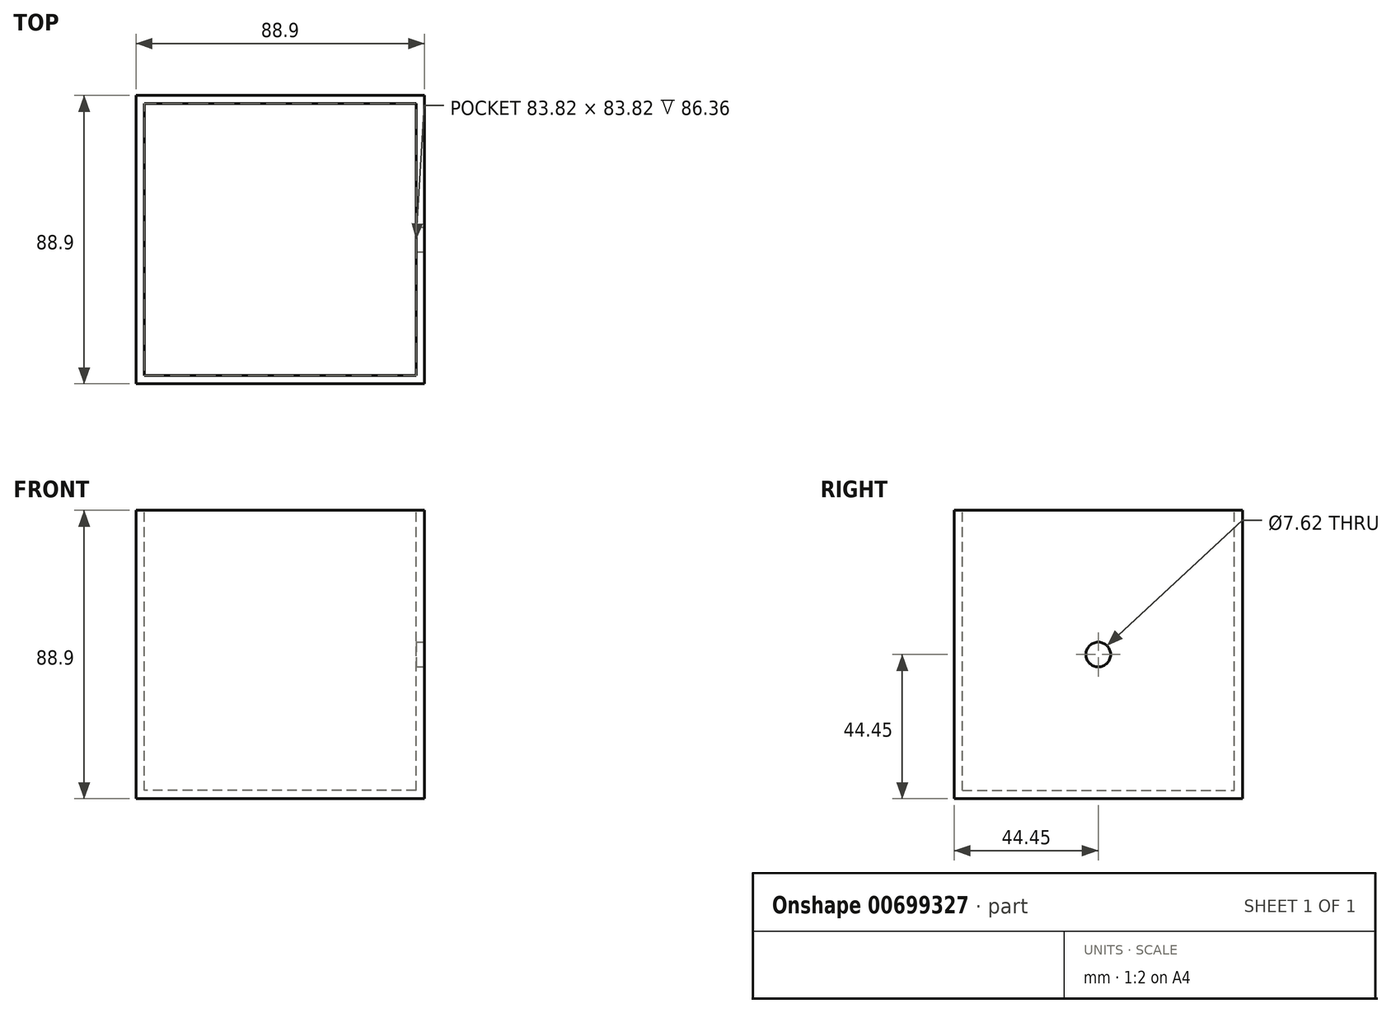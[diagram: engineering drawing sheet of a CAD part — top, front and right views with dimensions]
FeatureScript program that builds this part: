
annotation { "Feature Type Name" : "Feature", "Feature Type Description" : "" }
export const myFeature = defineFeature(function(context is Context, id is Id, definition is map)
    precondition{}
    {
        {
            var Q0;
            Q0=qCreatedBy(makeId("Front.planeOp"),FACE);
            var sketch = newSketch(context, id + "F0", { "sketchPlane" : qUnion([Q0])});
            skLineSegment(sketch, "E0.bottom", {"start": v(44.45, -44.45) * mm, "end": v(-44.45, -44.45) * mm});
            skLineSegment(sketch, "E0.top", {"start": v(44.45, 44.45) * mm, "end": v(-44.45, 44.45) * mm});
            skLineSegment(sketch, "E0.left", {"start": v(44.45, -44.45) * mm, "end": v(44.45, 44.45) * mm});
            skLineSegment(sketch, "E0.right", {"start": v(-44.45, -44.45) * mm, "end": v(-44.45, 44.45) * mm});
            skPoint(sketch, "E0.middle", {"position": v(0, 0) * mm});
            skSolve(sketch);
        }
        {
            var Q0;
            Q0 = qSketchRegion(id + "F0", true);
            extrude(context, id + "F1", {"entities" : qUnion([Q0]), "depth" : 88.9 * mm, "offsetDistance" : 25.4 * mm});
        }
        {
            var Q0;
            Q0=makeQuery(id+"F1.opExtrude","SWEPT_FACE",FACE,{"disambiguationData":[OSD([sQuery(id+"F0.wireOp",EDGE,"E0.top")])]});
            shell(context, id + "F2", {"entities" : qUnion([Q0]), "thickness" : 2.54 * mm});
        }
        {
            var Q0;
            Q0=makeQuery(id+"F1.opExtrude","SWEPT_FACE",FACE,{"disambiguationData":[OSD([sQuery(id+"F0.wireOp",EDGE,"E0.left")])]});
            var sketch = newSketch(context, id + "F3", { "sketchPlane" : qUnion([Q0])});
            skCircle(sketch, "E1", {"center": v(-44.45, 0) * mm, "radius": 3.81 * mm});
            skSolve(sketch);
        }
        {
            var Q0;
            Q0 = qSketchRegion(id + "F3", true);
            extrude(context, id + "F4", {"entities" : qUnion([Q0]), "operationType" : NewBodyOperationType.REMOVE, "oppositeDirection" : true, "depth" : 25.4 * mm, "offsetDistance" : 25.4 * mm});
        }
    });
